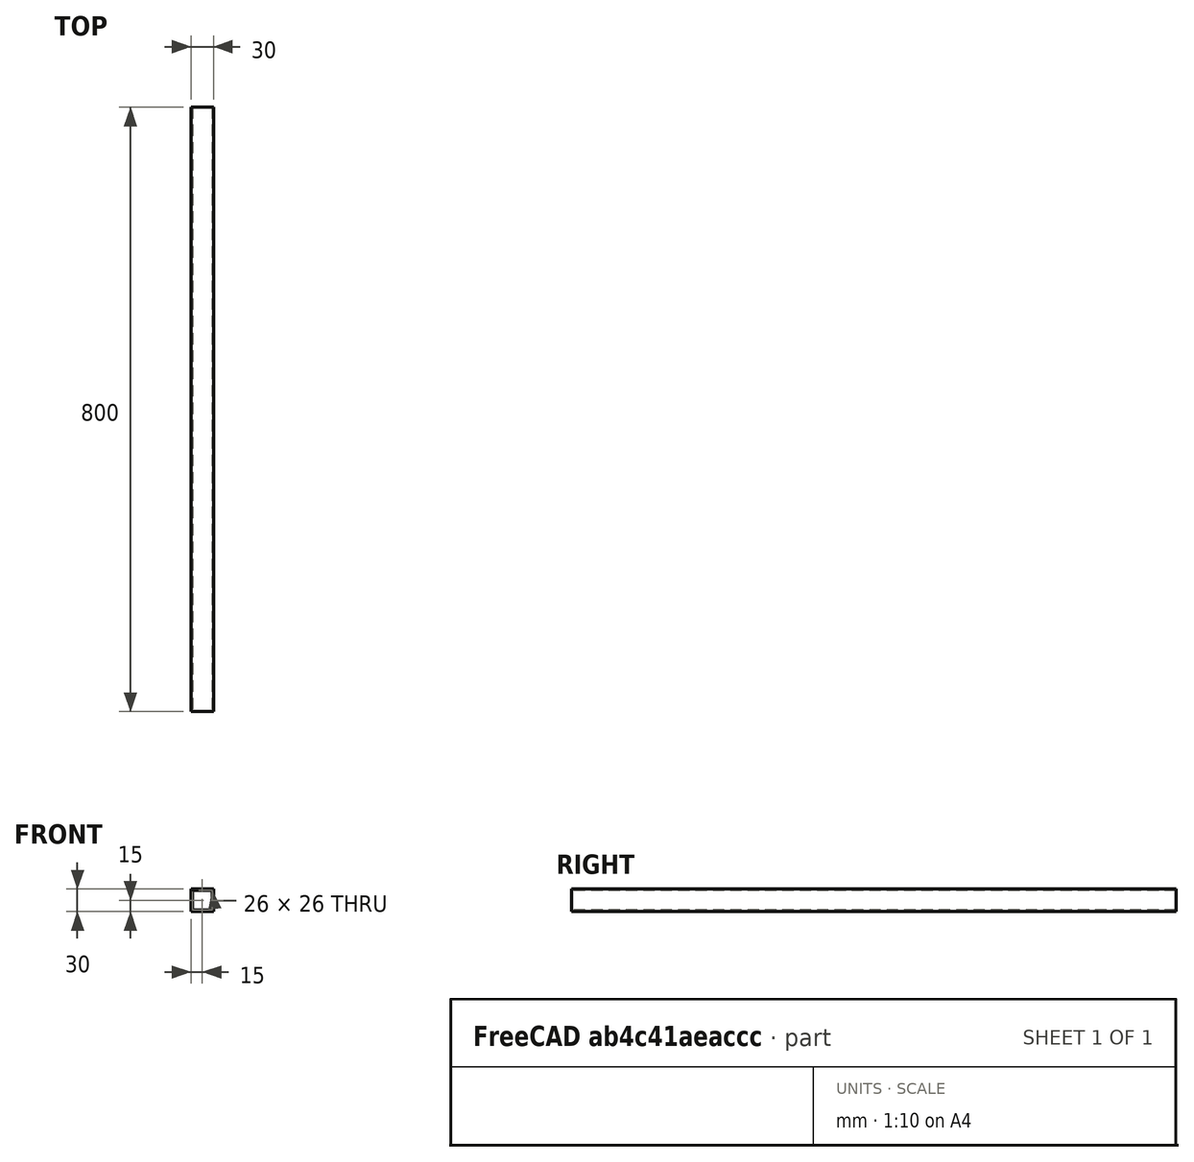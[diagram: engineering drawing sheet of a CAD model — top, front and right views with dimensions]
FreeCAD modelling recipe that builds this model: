
FCSTD DOCUMENT  (FreeCAD 0.20R29177 +426 (Git))
Label: beam_cross_bottom
License: All rights reserved
LicenseURL: http://en.wikipedia.org/wiki/All_rights_reserved
objects: Sketcher::SketchObject×1, PartDesign::Pad×1, PartDesign::Body×1
note: 4 computed .brp shape members not serialized (recipe doc carries the construction recipe); baked Part::Feature solids carry a one-line shape summary decoded from their .brp

FEATURE [Sketcher::SketchObject] Sketch
  FullyConstrained = true
  MapMode = 5
  Placement = pos=(0,0,0) rot=(1,0,0;1.5708rad)
  Support = -> [XZ_Plane]
  sketch-geometry (10):
    g0: LineSegment StartX=0 StartY=0 StartZ=0 EndX=30 EndY=0 EndZ=0
    g1: LineSegment StartX=30 StartY=0 StartZ=0 EndX=30 EndY=30 EndZ=0
    g2: LineSegment StartX=30 StartY=30 StartZ=0 EndX=0 EndY=30 EndZ=0
    g3: LineSegment StartX=0 StartY=30 StartZ=0 EndX=0 EndY=0 EndZ=0
    g4: LineSegment StartX=2 StartY=28 StartZ=0 EndX=28 EndY=28 EndZ=0
    g5: LineSegment StartX=28 StartY=28 StartZ=0 EndX=28 EndY=2 EndZ=0
    g6: LineSegment StartX=28 StartY=2 StartZ=0 EndX=2 EndY=2 EndZ=0
    g7: LineSegment StartX=2 StartY=2 StartZ=0 EndX=2 EndY=28 EndZ=0
    g8: LineSegment StartX=0 StartY=0 StartZ=0 EndX=30 EndY=30 EndZ=0
    g9: LineSegment StartX=0 StartY=30 StartZ=0 EndX=30 EndY=0 EndZ=0
  constraints (27):
    c: Coincident(g0,g1)
    c: Coincident(g1,g2)
    c: Coincident(g2,g3)
    c: Coincident(g3,g0)
    c: Horizontal(g0)
    c: Horizontal(g2)
    c: Vertical(g1)
    c: Vertical(g3)
    c: Coincident(g0,g-1)
    c: DistanceX(g2,g2) = 30
    c: Coincident(g4,g5)
    c: Coincident(g5,g6)
    c: Coincident(g6,g7)
    c: Coincident(g7,g4)
    c: Horizontal(g4)
    c: Horizontal(g6)
    c: Vertical(g5)
    c: Vertical(g7)
    c: DistanceY(g4,g1) = 2
    c: Equal(g1,g2)
    c: Equal(g4,g5)
    c: Coincident(g8,g0)
    c: Coincident(g8,g1)
    c: PointOnObject(g4,g8)
    c: Coincident(g9,g2)
    c: Coincident(g9,g0)
    c: PointOnObject(g4,g9)
FEATURE [PartDesign::Pad] Pad
  Direction = (0,-1,-2e-16)
  Length = 800
  Length2 = 10
  Placement = pos=(0,0,0) rot=(1,0,0;1.5708rad)
  Profile = -> Sketch
  ReferenceAxis = -> Sketch [N_Axis]
  Refine = true
  Type = 0
FEATURE [PartDesign::Body] Body
  Group = -> [Sketch,Pad]
  Origin = -> Origin
  Tip = -> Pad
